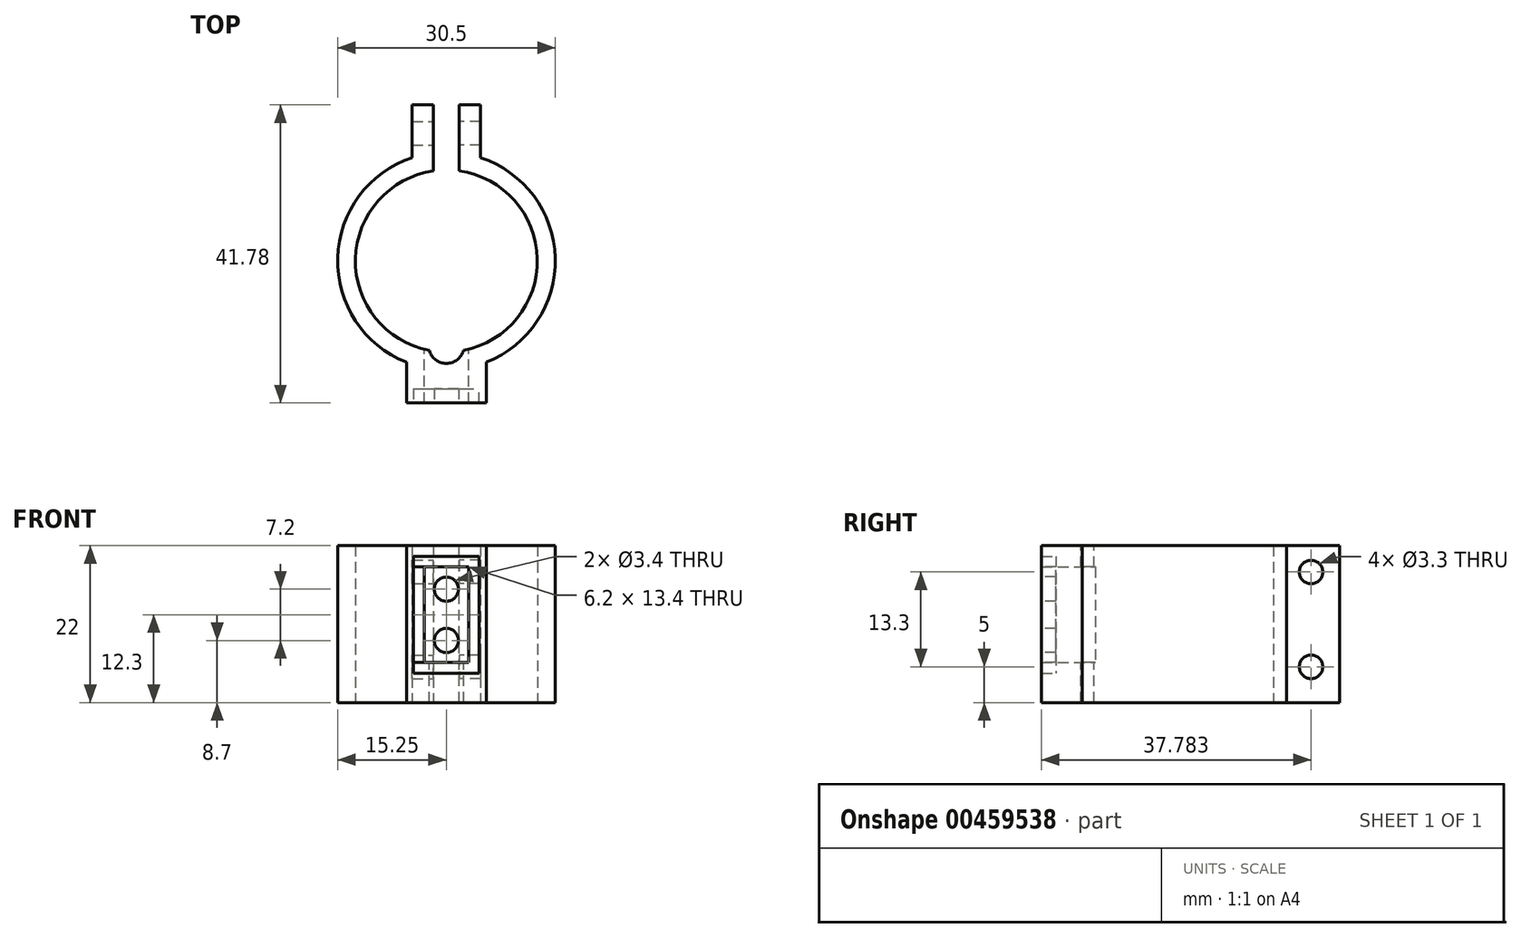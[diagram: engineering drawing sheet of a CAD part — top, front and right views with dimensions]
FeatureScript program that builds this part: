
annotation { "Feature Type Name" : "Feature", "Feature Type Description" : "" }
export const myFeature = defineFeature(function(context is Context, id is Id, definition is map)
    precondition{}
    {
        {
            var Q0;
            Q0=qCreatedBy(makeId("Top.planeOp"),FACE);
            var sketch = newSketch(context, id + "F0", { "sketchPlane" : qUnion([Q0])});
            skCircle(sketch, "E0", {"center": v(0, 0) * mm, "radius": 12.75 * mm});
            skCircle(sketch, "E1", {"center": v(0, 0) * mm, "radius": 15.25 * mm});
            skLineSegment(sketch, "E2.bottom", {"start": v(-1.8, 17.38) * mm, "end": v(1.8, 17.38) * mm});
            skLineSegment(sketch, "E2.top", {"start": v(-1.8, 10) * mm, "end": v(1.8, 10) * mm});
            skLineSegment(sketch, "E2.left", {"start": v(-1.8, 17.38) * mm, "end": v(-1.8, 10) * mm});
            skLineSegment(sketch, "E2.right", {"start": v(1.8, 17.38) * mm, "end": v(1.8, 10) * mm});
            skSolve(sketch);
        }
        {
            var Q0;
            {var subQ0=sQuery(id+"F0.wireOp",EDGE,"E2.left");var subQ1=sQuery(id+"F0.wireOp",EDGE,"E0");var subQ2=makeQuery(id+"F0.imprint","INTERSECT",VERTEX,{"derivedFrom":[subQ1,subQ0]});Q0=makeQuery(id+"F0.imprint","IMPRINT",FACE,{"disambiguationData":[TD([[makeQuery(id+"F0.imprint","IMPRINT",EDGE,{"disambiguationData":[TD([[subQ2,-1.0]])],"derivedFrom":subQ1}),-1.0]])]});}
            extrude(context, id + "F1", {"entities" : qUnion([Q0]), "depth" : 29 * mm});
        }
        {
            var Q0;
            Q0=makeQuery(id+"F1.opExtrude","SWEPT_FACE",FACE,{"disambiguationData":[OSD([sQuery(id+"F0.wireOp",EDGE,"E2.left")])]});
            var sketch = newSketch(context, id + "F2", { "sketchPlane" : qUnion([Q0])});
            skLineSegment(sketch, "E3.bottom", {"start": v(13.88, 29) * mm, "end": v(21.88, 29) * mm});
            skLineSegment(sketch, "E3.top", {"start": v(13.88, 0) * mm, "end": v(21.88, 0) * mm});
            skLineSegment(sketch, "E3.left", {"start": v(13.88, 29) * mm, "end": v(13.88, 0) * mm});
            skLineSegment(sketch, "E3.right", {"start": v(21.88, 29) * mm, "end": v(21.88, 0) * mm});
            skCircle(sketch, "E4", {"center": v(17.88, 18.3) * mm, "radius": 1.65 * mm});
            skPoint(sketch, "E5", {"position": v(17.88, 29) * mm});
            skPoint(sketch, "E6", {"position": v(21.88, 14.5) * mm});
            skCircle(sketch, "E7", {"center": v(17.88, 5) * mm, "radius": 1.65 * mm});
            skSolve(sketch);
        }
        {
            var Q0;
            {var subQ2=sQuery(id+"F2.wireOp",EDGE,"E3.right");Q0=makeQuery(id+"F2.imprint","IMPRINT",FACE,{"disambiguationData":[TD([[makeQuery(id+"F2.imprint","IMPRINT",EDGE,{"derivedFrom":subQ2}),-1.0]])]});}
            var Q1;
            {var subQ3=sQuery(id+"F2.wireOp",EDGE,"E3.left");Q1=makeQuery(id+"F2.imprint","IMPRINT",FACE,{"disambiguationData":[TD([[makeQuery(id+"F2.imprint","IMPRINT",EDGE,{"derivedFrom":subQ3}),1.0]])]});}
            extrude(context, id + "F3", {"entities" : qUnion([Q0, Q1]), "operationType" : NewBodyOperationType.ADD, "oppositeDirection" : true, "depth" : 3 * mm});
        }
        {
            var Q0;
            Q0=makeQuery(id+"F1.opExtrude","SWEPT_FACE",FACE,{"disambiguationData":[OSD([sQuery(id+"F0.wireOp",EDGE,"E2.right")])]});
            var sketch = newSketch(context, id + "F4", { "sketchPlane" : qUnion([Q0])});
            skLineSegment(sketch, "E8.bottom", {"start": v(-13.88, 0) * mm, "end": v(-21.88, 0) * mm});
            skLineSegment(sketch, "E8.top", {"start": v(-13.88, 29) * mm, "end": v(-21.88, 29) * mm});
            skLineSegment(sketch, "E8.left", {"start": v(-13.88, 0) * mm, "end": v(-13.88, 29) * mm});
            skLineSegment(sketch, "E8.right", {"start": v(-21.88, 0) * mm, "end": v(-21.88, 29) * mm});
            skCircle(sketch, "E9", {"center": v(-17.88, 18.3) * mm, "radius": 1.65 * mm});
            skCircle(sketch, "E10", {"center": v(-17.88, 5) * mm, "radius": 1.65 * mm});
            skPoint(sketch, "E11", {"position": v(-17.88, 29) * mm});
            skSolve(sketch);
        }
        {
            var Q0;
            {var subQ2=sQuery(id+"F4.wireOp",EDGE,"E8.right");Q0=makeQuery(id+"F4.imprint","IMPRINT",FACE,{"disambiguationData":[TD([[makeQuery(id+"F4.imprint","IMPRINT",EDGE,{"derivedFrom":subQ2}),-1.0]])]});}
            var Q1;
            {var subQ3=sQuery(id+"F4.wireOp",EDGE,"E8.left");Q1=makeQuery(id+"F4.imprint","IMPRINT",FACE,{"disambiguationData":[TD([[makeQuery(id+"F4.imprint","IMPRINT",EDGE,{"derivedFrom":subQ3}),1.0]])]});}
            extrude(context, id + "F5", {"entities" : qUnion([Q0, Q1]), "operationType" : NewBodyOperationType.ADD, "oppositeDirection" : true, "depth" : 3 * mm});
        }
        {
            var Q0;
            Q0=qCreatedBy(makeId("Front.planeOp"),FACE);
            cPlane(context, id + "F6", {"entities" : qUnion([Q0]), "cplaneType" : CPlaneType.OFFSET, "offset" : 13.8 * mm, "width" : 150 * mm, "height" : 150 * mm});
        }
        {
            var Q0;
            Q0=qCreatedBy(id+"F6.planeOp",FACE);
            var sketch = newSketch(context, id + "F7", { "sketchPlane" : qUnion([Q0])});
            skLineSegment(sketch, "E12.bottom", {"start": v(-3.1, 19) * mm, "end": v(3.1, 19) * mm});
            skLineSegment(sketch, "E12.top", {"start": v(-3.1, 5.6) * mm, "end": v(3.1, 5.6) * mm});
            skLineSegment(sketch, "E12.left", {"start": v(-3.1, 19) * mm, "end": v(-3.1, 5.6) * mm});
            skLineSegment(sketch, "E12.right", {"start": v(3.1, 19) * mm, "end": v(3.1, 5.6) * mm});
            skSolve(sketch);
        }
        {
            var Q0;
            Q0=qCreatedBy(id+"F6.planeOp",FACE);
            var sketch = newSketch(context, id + "F8", { "sketchPlane" : qUnion([Q0])});
            skLineSegment(sketch, "E13.0", {"start": v(-5.6, 21.5) * mm, "end": v(5.6, 21.5) * mm});
            skLineSegment(sketch, "E13.1", {"start": v(-5.6, 21.5) * mm, "end": v(-5.6, 3.1) * mm});
            skLineSegment(sketch, "E13.2", {"start": v(-5.6, 3.1) * mm, "end": v(5.6, 3.1) * mm});
            skLineSegment(sketch, "E13.3", {"start": v(5.6, 21.5) * mm, "end": v(5.6, 3.1) * mm});
            skLineSegment(sketch, "E14.0", {"start": v(-3.1, 19) * mm, "end": v(-3.1, 5.6) * mm});
            skLineSegment(sketch, "E14.1", {"start": v(-3.1, 19) * mm, "end": v(3.1, 19) * mm});
            skLineSegment(sketch, "E14.2", {"start": v(3.1, 19) * mm, "end": v(3.1, 5.6) * mm});
            skLineSegment(sketch, "E14.3", {"start": v(-3.1, 5.6) * mm, "end": v(3.1, 5.6) * mm});
            skSolve(sketch);
        }
        {
            var Q0;
            Q0 = qSketchRegion(id + "F7", true);
            extrude(context, id + "F9", {"entities" : qUnion([Q0]), "operationType" : NewBodyOperationType.REMOVE, "depth" : 25 * mm});
        }
        {
            var Q0;
            Q0 = qSketchRegion(id + "F8", true);
            extrude(context, id + "F10", {"entities" : qUnion([Q0]), "operationType" : NewBodyOperationType.ADD, "depth" : 4.1 * mm});
        }
        {
            var Q0;
            Q0=makeQuery(id+"F9.boolean.opBoolean","COPY",FACE,{"derivedFrom":makeQuery(id+"F9.opExtrude","CAP_FACE",FACE,{"disambiguationData":[OSD([sQuery(id+"F7.wireOp",EDGE,"E12.bottom"),sQuery(id+"F7.wireOp",EDGE,"E12.top"),sQuery(id+"F7.wireOp",EDGE,"E12.left"),sQuery(id+"F7.wireOp",EDGE,"E12.right")])],"isStart":true})});
            extrude(context, id + "F11", {"entities" : qUnion([Q0]), "operationType" : NewBodyOperationType.REMOVE, "oppositeDirection" : true, "depth" : 25 * mm});
        }
        {
            var Q0;
            Q0=makeQuery(id+"F10.opExtrude","CAP_FACE",FACE,{"disambiguationData":[OSD([sQuery(id+"F8.wireOp",EDGE,"E13.0"),sQuery(id+"F8.wireOp",EDGE,"E13.1"),sQuery(id+"F8.wireOp",EDGE,"E13.2"),sQuery(id+"F8.wireOp",EDGE,"E13.3"),sQuery(id+"F8.wireOp",EDGE,"E14.0"),sQuery(id+"F8.wireOp",EDGE,"E14.1"),sQuery(id+"F8.wireOp",EDGE,"E14.2"),sQuery(id+"F8.wireOp",EDGE,"E14.3")])],"isStart":false});
            var sketch = newSketch(context, id + "F12", { "sketchPlane" : qUnion([Q0])});
            skLineSegment(sketch, "E15.0", {"start": v(4.6, 20.5) * mm, "end": v(4.6, 4.1) * mm});
            skLineSegment(sketch, "E15.1", {"start": v(-4.6, 20.5) * mm, "end": v(4.6, 20.5) * mm});
            skLineSegment(sketch, "E15.2", {"start": v(-4.6, 20.5) * mm, "end": v(-4.6, 4.1) * mm});
            skLineSegment(sketch, "E15.3", {"start": v(-4.6, 4.1) * mm, "end": v(4.6, 4.1) * mm});
            skSolve(sketch);
        }
        {
            var Q0;
            Q0=makeQuery(id+"F12.imprint","IMPRINT",FACE,{"disambiguationData":[TD([[makeQuery(id+"F12.imprint","IMPRINT",EDGE,{"derivedFrom":sQuery(id+"F12.wireOp",EDGE,"E15.0")}),-1.0]])]});
            extrude(context, id + "F13", {"entities" : qUnion([Q0]), "depth" : 2 * mm});
        }
        {
            var Q0;
            Q0=makeQuery(id+"F13.opExtrude","SWEPT_FACE",FACE,{"disambiguationData":[OSD([sQuery(id+"F8.wireOp",EDGE,"E14.2")])]});
            var Q1;
            Q1=makeQuery(id+"F13.opExtrude","SWEPT_FACE",FACE,{"disambiguationData":[OSD([sQuery(id+"F12.wireOp",EDGE,"E15.2")])]});
            extrude(context, id + "F14", {"entities" : qUnion([Q0]), "endBound" : BoundingType.UP_TO_SURFACE, "endBoundEntityFace" : qUnion([Q1]), "depth" : 25 * mm});
        }
        {
            var Q0;
            {var subQ0=sQuery(id+"F8.wireOp",EDGE,"E14.2");Q0=makeQuery(id+"F14.opExtrude","SWEPT_FACE",FACE,{"disambiguationData":[OSD([subQ0]),TDD([makeQuery(id+"F13.opExtrude","CAP_EDGE",EDGE,{"disambiguationData":[OSD([subQ0])],"isStart":false})])]});}
            var sketch = newSketch(context, id + "F15", { "sketchPlane" : qUnion([Q0])});
            skCircle(sketch, "E16", {"center": v(0, 15.9) * mm, "radius": 1.7 * mm});
            skCircle(sketch, "E17", {"center": v(0, 8.7) * mm, "radius": 1.7 * mm});
            skSolve(sketch);
        }
        {
            var Q0;
            Q0=makeQuery(id+"F15.imprint","IMPRINT",FACE,{"disambiguationData":[TD([[makeQuery(id+"F15.imprint","IMPRINT",EDGE,{"derivedFrom":sQuery(id+"F15.wireOp",EDGE,"E16")}),1.0]])]});
            var Q1;
            Q1=makeQuery(id+"F15.imprint","IMPRINT",FACE,{"disambiguationData":[TD([[makeQuery(id+"F15.imprint","IMPRINT",EDGE,{"derivedFrom":sQuery(id+"F15.wireOp",EDGE,"E17")}),1.0]])]});
            extrude(context, id + "F16", {"entities" : qUnion([Q0, Q1]), "operationType" : NewBodyOperationType.REMOVE, "oppositeDirection" : true, "depth" : 25 * mm});
        }
        {
            var Q0;
            Q0=makeQuery(id+"F10.opExtrude","CAP_FACE",FACE,{"disambiguationData":[OSD([sQuery(id+"F8.wireOp",EDGE,"E13.0"),sQuery(id+"F8.wireOp",EDGE,"E13.1"),sQuery(id+"F8.wireOp",EDGE,"E13.2"),sQuery(id+"F8.wireOp",EDGE,"E13.3"),sQuery(id+"F8.wireOp",EDGE,"E14.0"),sQuery(id+"F8.wireOp",EDGE,"E14.1"),sQuery(id+"F8.wireOp",EDGE,"E14.2"),sQuery(id+"F8.wireOp",EDGE,"E14.3")])],"isStart":false});
            var Q1;
            Q1=makeQuery(id+"F13.opExtrude","CAP_FACE",FACE,{"disambiguationData":[OSD([sQuery(id+"F8.wireOp",EDGE,"E14.0"),sQuery(id+"F8.wireOp",EDGE,"E14.1"),sQuery(id+"F8.wireOp",EDGE,"E14.2"),sQuery(id+"F8.wireOp",EDGE,"E14.3"),sQuery(id+"F12.wireOp",EDGE,"E15.0"),sQuery(id+"F12.wireOp",EDGE,"E15.1"),sQuery(id+"F12.wireOp",EDGE,"E15.2"),sQuery(id+"F12.wireOp",EDGE,"E15.3")])],"isStart":false});
            extrude(context, id + "F17", {"entities" : qUnion([Q0]), "endBound" : BoundingType.UP_TO_SURFACE, "endBoundEntityFace" : qUnion([Q1]), "depth" : 25 * mm});
        }
        {
            var Q0;
            Q0=makeQuery(id+"F5.boolean.opBoolean","MERGE",FACE,{"derivedFrom":[makeQuery(id+"F3.boolean.opBoolean","MERGE",FACE,{"derivedFrom":[makeQuery(id+"F1.opExtrude","CAP_FACE",FACE,{"disambiguationData":[OSD([sQuery(id+"F0.wireOp",EDGE,"E0"),sQuery(id+"F0.wireOp",EDGE,"E1"),sQuery(id+"F0.wireOp",EDGE,"E2.left"),sQuery(id+"F0.wireOp",EDGE,"E2.right")])],"isStart":false}),makeQuery(id+"F3.opExtrude","SWEPT_FACE",FACE,{"disambiguationData":[OSD([sQuery(id+"F2.wireOp",EDGE,"E3.bottom")])]})]}),makeQuery(id+"F5.opExtrude","SWEPT_FACE",FACE,{"disambiguationData":[OSD([sQuery(id+"F4.wireOp",EDGE,"E8.top")])]})]});
            var sketch = newSketch(context, id + "F18", { "sketchPlane" : qUnion([Q0])});
            skCircle(sketch, "E18", {"center": v(0, -11.85) * mm, "radius": 2.5 * mm});
            skPoint(sketch, "E19", {"position": v(0, -12.75) * mm});
            skSolve(sketch);
        }
        {
            var Q0;
            {var subQ0=sQuery(id+"F18.wireOp",EDGE,"E18");var subQ1=makeQuery(id+"F1.opExtrude","CAP_EDGE",EDGE,{"disambiguationData":[OSD([sQuery(id+"F0.wireOp",EDGE,"E0")])],"isStart":false});var subQ2=makeQuery(id+"F18.imprint","INTERSECT",VERTEX,{"disambiguationData":[OD(0.0)],"derivedFrom":[subQ1,subQ0]});Q0=makeQuery(id+"F18.imprint","IMPRINT",FACE,{"disambiguationData":[TD([[makeQuery(id+"F18.imprint","IMPRINT",EDGE,{"disambiguationData":[TD([[subQ2,-1.0]])],"derivedFrom":subQ0}),1.0]])]});}
            var Q1;
            Q1=makeQuery(id+"F5.boolean.opBoolean","MERGE",FACE,{"derivedFrom":[makeQuery(id+"F3.boolean.opBoolean","MERGE",FACE,{"derivedFrom":[makeQuery(id+"F1.opExtrude","CAP_FACE",FACE,{"disambiguationData":[OSD([sQuery(id+"F0.wireOp",EDGE,"E0"),sQuery(id+"F0.wireOp",EDGE,"E1"),sQuery(id+"F0.wireOp",EDGE,"E2.left"),sQuery(id+"F0.wireOp",EDGE,"E2.right")])],"isStart":true}),makeQuery(id+"F3.opExtrude","SWEPT_FACE",FACE,{"disambiguationData":[OSD([sQuery(id+"F2.wireOp",EDGE,"E3.top")])]})]}),makeQuery(id+"F5.opExtrude","SWEPT_FACE",FACE,{"disambiguationData":[OSD([sQuery(id+"F4.wireOp",EDGE,"E8.bottom")])]})]});
            extrude(context, id + "F19", {"entities" : qUnion([Q0]), "operationType" : NewBodyOperationType.REMOVE, "endBound" : BoundingType.UP_TO_SURFACE, "oppositeDirection" : true, "endBoundEntityFace" : qUnion([Q1]), "depth" : 25 * mm});
        }
        {
            var Q0;
            Q0=makeQuery(id+"F17.opExtrude","SWEPT_FACE",FACE,{"disambiguationData":[OSD([sQuery(id+"F8.wireOp",EDGE,"E13.2")])]});
            var Q1;
            Q1=makeQuery(id+"F10.opExtrude","SWEPT_FACE",FACE,{"disambiguationData":[OSD([sQuery(id+"F8.wireOp",EDGE,"E13.2")])]});
            var Q2;
            Q2=makeQuery(id+"F5.boolean.opBoolean","MERGE",FACE,{"derivedFrom":[makeQuery(id+"F3.boolean.opBoolean","MERGE",FACE,{"derivedFrom":[makeQuery(id+"F1.opExtrude","CAP_FACE",FACE,{"disambiguationData":[OSD([sQuery(id+"F0.wireOp",EDGE,"E0"),sQuery(id+"F0.wireOp",EDGE,"E1"),sQuery(id+"F0.wireOp",EDGE,"E2.left"),sQuery(id+"F0.wireOp",EDGE,"E2.right")])],"isStart":true}),makeQuery(id+"F3.opExtrude","SWEPT_FACE",FACE,{"disambiguationData":[OSD([sQuery(id+"F2.wireOp",EDGE,"E3.top")])]})]}),makeQuery(id+"F5.opExtrude","SWEPT_FACE",FACE,{"disambiguationData":[OSD([sQuery(id+"F4.wireOp",EDGE,"E8.bottom")])]})]});
            extrude(context, id + "F20", {"entities" : qUnion([Q0, Q1]), "operationType" : NewBodyOperationType.ADD, "endBound" : BoundingType.UP_TO_SURFACE, "endBoundEntityFace" : qUnion([Q2]), "depth" : 25 * mm});
        }
        {
            var Q0;
            {var subQ0=sQuery(id+"F8.wireOp",EDGE,"E13.0");Q0=makeQuery(id+"F20.boolean.opBoolean","MERGE",FACE,{"derivedFrom":[makeQuery(id+"F10.opExtrude","SWEPT_FACE",FACE,{"disambiguationData":[OSD([subQ0])]}),makeQuery(id+"F17.opExtrude","SWEPT_FACE",FACE,{"disambiguationData":[OSD([subQ0])]})]});}
            var Q1;
            Q1=makeQuery(id+"F5.boolean.opBoolean","MERGE",FACE,{"derivedFrom":[makeQuery(id+"F3.boolean.opBoolean","MERGE",FACE,{"derivedFrom":[makeQuery(id+"F1.opExtrude","CAP_FACE",FACE,{"disambiguationData":[OSD([sQuery(id+"F0.wireOp",EDGE,"E0"),sQuery(id+"F0.wireOp",EDGE,"E1"),sQuery(id+"F0.wireOp",EDGE,"E2.left"),sQuery(id+"F0.wireOp",EDGE,"E2.right")])],"isStart":false}),makeQuery(id+"F3.opExtrude","SWEPT_FACE",FACE,{"disambiguationData":[OSD([sQuery(id+"F2.wireOp",EDGE,"E3.bottom")])]})]}),makeQuery(id+"F5.opExtrude","SWEPT_FACE",FACE,{"disambiguationData":[OSD([sQuery(id+"F4.wireOp",EDGE,"E8.top")])]})]});
            extrude(context, id + "F21", {"entities" : qUnion([Q0]), "operationType" : NewBodyOperationType.ADD, "endBound" : BoundingType.UP_TO_SURFACE, "endBoundEntityFace" : qUnion([Q1]), "depth" : 25 * mm});
        }
        {
            var Q0;
            {var subQ0=sQuery(id+"F4.wireOp",EDGE,"E8.top");var subQ1=sQuery(id+"F2.wireOp",EDGE,"E3.bottom");var subQ2=sQuery(id+"F0.wireOp",EDGE,"E2.right");var subQ3=sQuery(id+"F0.wireOp",EDGE,"E2.left");var subQ4=sQuery(id+"F0.wireOp",EDGE,"E1");var subQ5=sQuery(id+"F0.wireOp",EDGE,"E0");Q0=makeQuery(id+"F21.boolean.opBoolean","MERGE",FACE,{"derivedFrom":[makeQuery(id+"F5.boolean.opBoolean","MERGE",FACE,{"derivedFrom":[makeQuery(id+"F3.boolean.opBoolean","MERGE",FACE,{"derivedFrom":[makeQuery(id+"F1.opExtrude","CAP_FACE",FACE,{"disambiguationData":[OSD([subQ5,subQ4,subQ3,subQ2])],"isStart":false}),makeQuery(id+"F3.opExtrude","SWEPT_FACE",FACE,{"disambiguationData":[OSD([subQ1])]})]}),makeQuery(id+"F5.opExtrude","SWEPT_FACE",FACE,{"disambiguationData":[OSD([subQ0])]})]}),makeQuery(id+"F21.opExtrude","CAP_FACE",FACE,{"disambiguationData":[OSD([subQ5,subQ4,subQ3,subQ2,subQ1,subQ0])],"isStart":false})]});}
            extrude(context, id + "F22", {"entities" : qUnion([Q0]), "operationType" : NewBodyOperationType.REMOVE, "oppositeDirection" : true, "depth" : 7 * mm});
        }
    });
